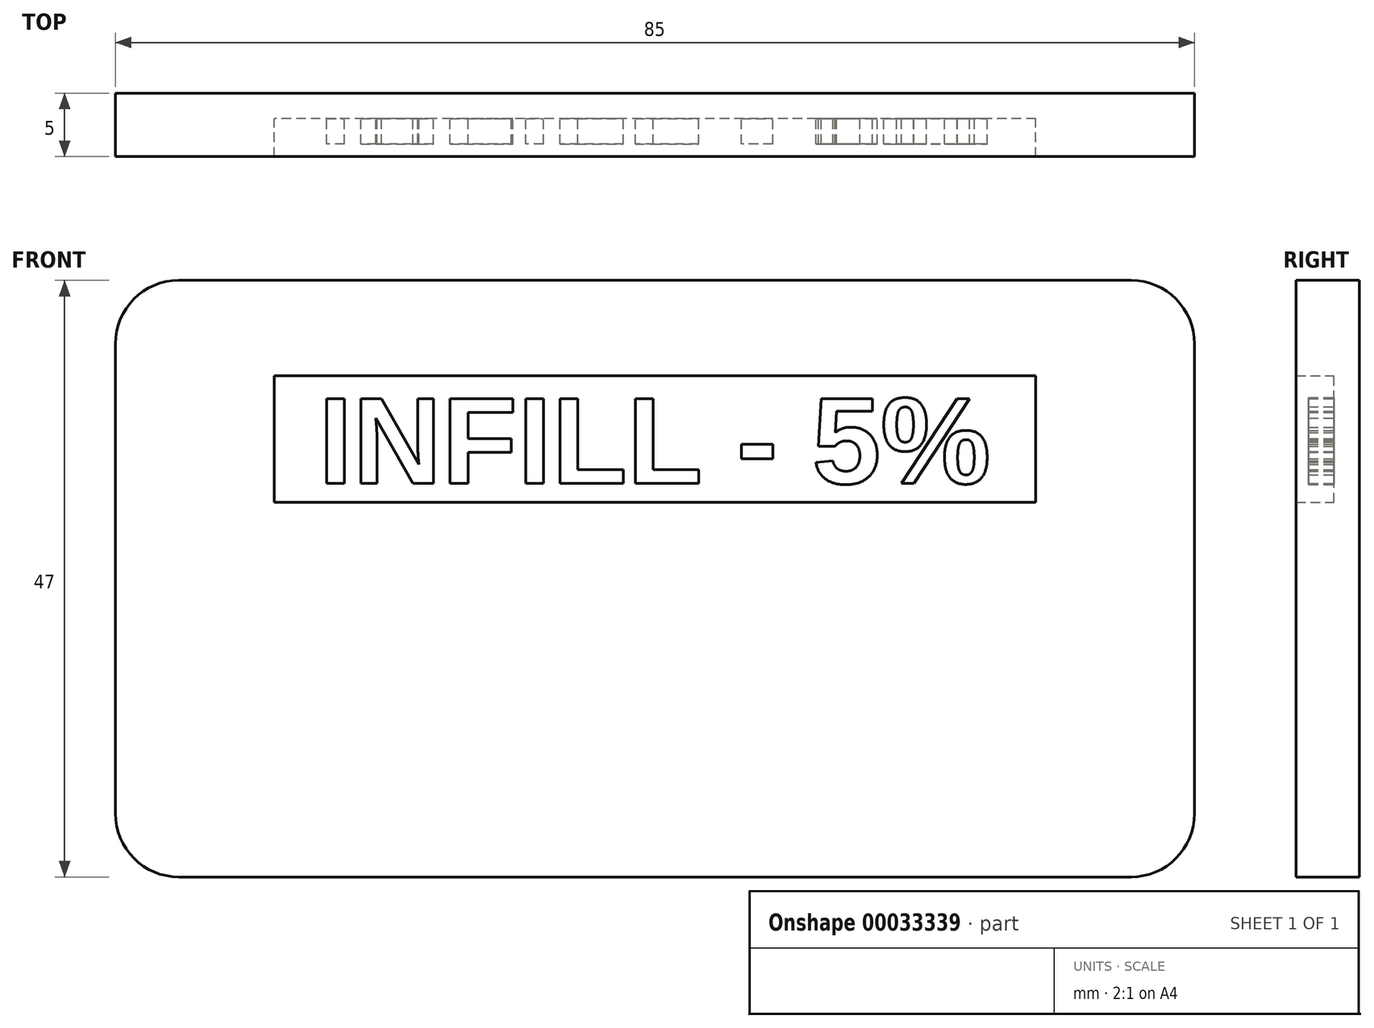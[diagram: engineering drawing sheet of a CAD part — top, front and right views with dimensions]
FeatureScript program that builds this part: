
annotation { "Feature Type Name" : "Feature", "Feature Type Description" : "" }
export const myFeature = defineFeature(function(context is Context, id is Id, definition is map)
    precondition{}
    {
        {
            var Q0;
            Q0=qCreatedBy(makeId("Front.planeOp"),FACE);
            var sketch = newSketch(context, id + "F0", { "sketchPlane" : qUnion([Q0])});
            skLineSegment(sketch, "E0.rect.bottom", {"start": v(42.5, -23.5) * mm, "end": v(-42.5, -23.5) * mm});
            skLineSegment(sketch, "E0.rect.top", {"start": v(42.5, 23.5) * mm, "end": v(-42.5, 23.5) * mm});
            skLineSegment(sketch, "E0.rect.left", {"start": v(42.5, -23.5) * mm, "end": v(42.5, 23.5) * mm});
            skLineSegment(sketch, "E0.rect.right", {"start": v(-42.5, -23.5) * mm, "end": v(-42.5, 23.5) * mm});
            skPoint(sketch, "E0.rect.middle", {"position": v(0, 0) * mm});
            skPoint(sketch, "E1.visualSharp", {"position": v(-42.5, 23.5) * mm});
            skLineSegment(sketch, "E1.filletArc", {"start": v(-42.5, 23.5) * mm, "end": v(-42.5, 23.5) * mm});
            skPoint(sketch, "E2.visualSharp", {"position": v(-42.5, -23.5) * mm});
            skLineSegment(sketch, "E2.filletArc", {"start": v(-42.5, -23.5) * mm, "end": v(-42.5, -23.5) * mm});
            skPoint(sketch, "E3.visualSharp", {"position": v(42.5, -23.5) * mm});
            skLineSegment(sketch, "E3.filletArc", {"start": v(42.5, -23.5) * mm, "end": v(42.5, -23.5) * mm});
            skPoint(sketch, "E4.visualSharp", {"position": v(42.5, 23.5) * mm});
            skLineSegment(sketch, "E4.filletArc", {"start": v(42.5, 23.5) * mm, "end": v(42.5, 23.5) * mm});
            skLineSegment(sketch, "E5.rect.bottom", {"start": v(30, 6) * mm, "end": v(-30, 6) * mm});
            skLineSegment(sketch, "E5.rect.top", {"start": v(30, 16) * mm, "end": v(-30, 16) * mm});
            skLineSegment(sketch, "E5.rect.left", {"start": v(30, 6) * mm, "end": v(30, 16) * mm});
            skLineSegment(sketch, "E5.rect.right", {"start": v(-30, 6) * mm, "end": v(-30, 16) * mm});
            skPoint(sketch, "E5.rect.middle", {"position": v(0, 11) * mm});
            skSolve(sketch);
        }
        {
            var Q0;
            Q0=makeQuery(id+"F0.imprint","IMPRINT",FACE,{"disambiguationData":[TD([[makeQuery(id+"F0.imprint","IMPRINT",EDGE,{"derivedFrom":sQuery(id+"F0.wireOp",EDGE,"E0.rect.bottom")}),-1.0]])]});
            extrude(context, id + "F1", {"entities" : qUnion([Q0]), "depth" : 5 * mm});
        }
        {
            var Q0;
            Q0=makeQuery(id+"F0.imprint","IMPRINT",FACE,{"disambiguationData":[TD([[makeQuery(id+"F0.imprint","IMPRINT",EDGE,{"derivedFrom":sQuery(id+"F0.wireOp",EDGE,"E5.rect.bottom")}),-1.0]])]});
            extrude(context, id + "F2", {"entities" : qUnion([Q0]), "operationType" : NewBodyOperationType.ADD, "depth" : 2 * mm});
        }
        {
            var Q0;
            Q0=makeQuery(id+"F2.opExtrude","CAP_FACE",FACE,{"disambiguationData":[OSD([sQuery(id+"F0.wireOp",EDGE,"E5.rect.bottom"),sQuery(id+"F0.wireOp",EDGE,"E5.rect.top"),sQuery(id+"F0.wireOp",EDGE,"E5.rect.left"),sQuery(id+"F0.wireOp",EDGE,"E5.rect.right")])],"isStart":false});
            var sketch = newSketch(context, id + "F3", { "sketchPlane" : qUnion([Q0])});
            skLineSegment(sketch, "E6", {"start": v(-30, 14.5) * mm, "end": v(30, 14.5) * mm, "construction": true});
            skLineSegment(sketch, "E7", {"start": v(-30, 7.5) * mm, "end": v(30, 7.5) * mm, "construction": true});
            skLineSegment(sketch, "E8", {"start": v(-26.5, 16) * mm, "end": v(-26.5, 6) * mm, "construction": true});
            skLineSegment(sketch, "E9", {"start": v(26.5, 16) * mm, "end": v(26.5, 6) * mm, "construction": true});
            skText(sketch, "E10", { "text": "INFILL - 5%", "fontName": "Arimo-Bold.ttf"});
            const initialGuessF3  = {"E10": [-0.0265, 0.0075, 1, 0, 0.007]};
            skSetInitialGuess(sketch, initialGuessF3);
            skSolve(sketch);
        }
        {
            var Q0;
            Q0 = qSketchRegion(id + "F3", true);
            extrude(context, id + "F4", {"entities" : qUnion([Q0]), "operationType" : NewBodyOperationType.ADD, "depth" : 2 * mm});
        }
        {
            var Q0;
            Q0=makeQuery(id+"F1.opExtrude","SWEPT_EDGE",EDGE,{"disambiguationData":[OSD([sQuery(id+"F0.wireOp",EDGE,"E0.rect.top"),sQuery(id+"F0.wireOp",EDGE,"E0.rect.right")])]});
            var Q1;
            Q1=makeQuery(id+"F1.opExtrude","SWEPT_EDGE",EDGE,{"disambiguationData":[OSD([sQuery(id+"F0.wireOp",EDGE,"E0.rect.bottom"),sQuery(id+"F0.wireOp",EDGE,"E0.rect.right")])]});
            var Q2;
            Q2=makeQuery(id+"F1.opExtrude","SWEPT_EDGE",EDGE,{"disambiguationData":[OSD([sQuery(id+"F0.wireOp",EDGE,"E0.rect.top"),sQuery(id+"F0.wireOp",EDGE,"E0.rect.left")])]});
            var Q3;
            Q3=makeQuery(id+"F1.opExtrude","SWEPT_EDGE",EDGE,{"disambiguationData":[OSD([sQuery(id+"F0.wireOp",EDGE,"E0.rect.bottom"),sQuery(id+"F0.wireOp",EDGE,"E0.rect.left")])]});
            fillet(context, id + "F5", {"entities" : qUnion([Q0, Q1, Q2, Q3]), "radius" : 5 * mm, "tangentPropagation" : true, "allowEdgeOverflow" : false});
        }
    });
